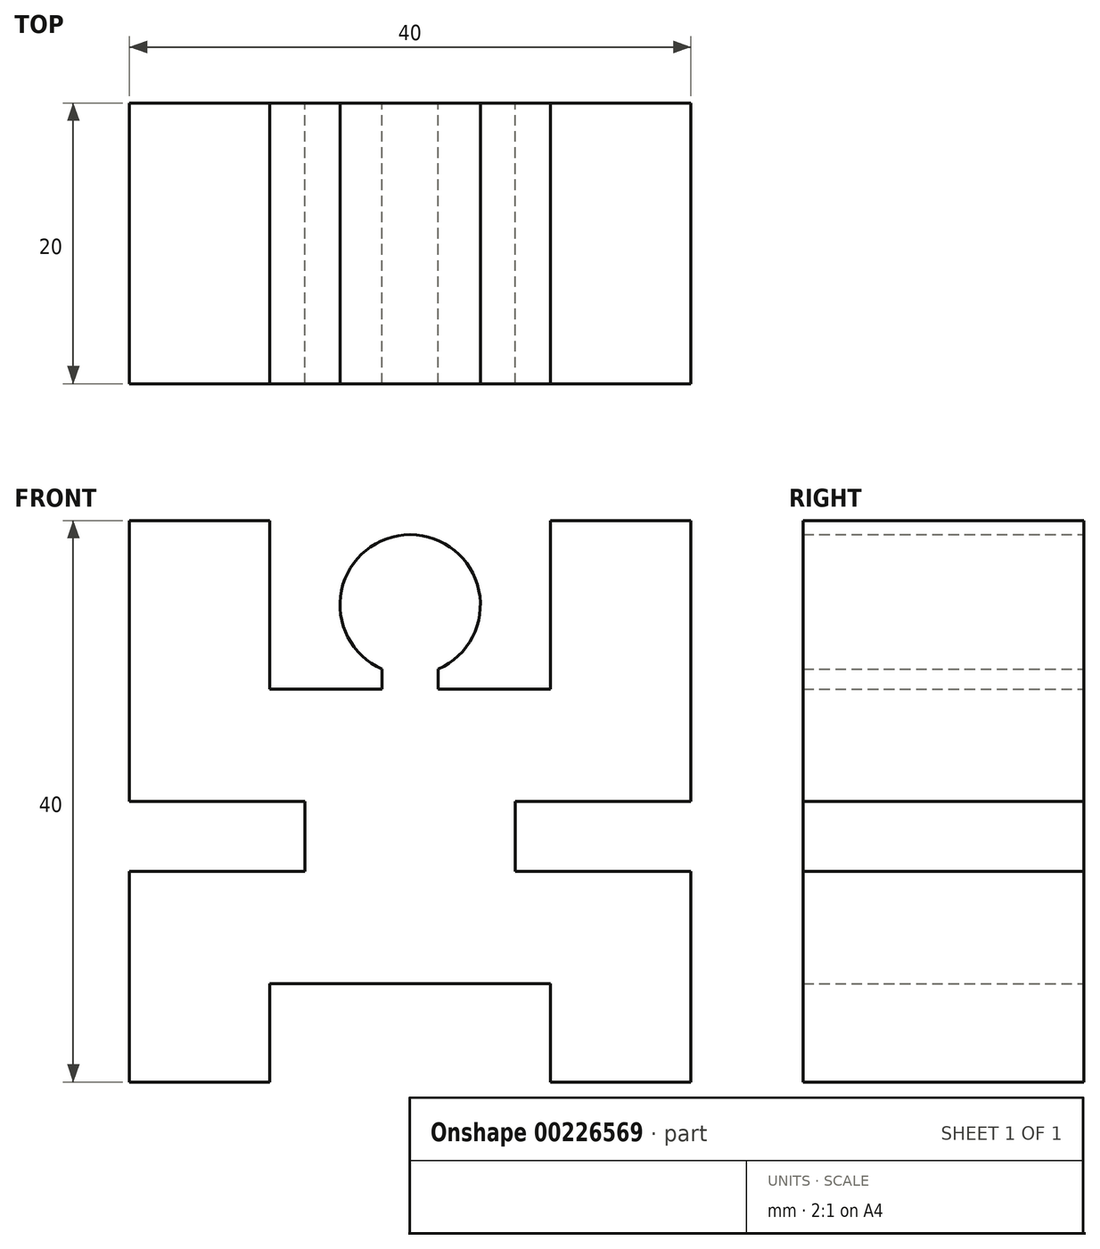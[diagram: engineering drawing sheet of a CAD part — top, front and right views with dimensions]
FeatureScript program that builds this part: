
annotation { "Feature Type Name" : "Feature", "Feature Type Description" : "" }
export const myFeature = defineFeature(function(context is Context, id is Id, definition is map)
    precondition{}
    {
        {
            var Q0;
            Q0=qCreatedBy(makeId("Front.planeOp"),FACE);
            var sketch = newSketch(context, id + "F0", { "sketchPlane" : qUnion([Q0])});
            skLineSegment(sketch, "E0", {"start": v(-2, 9.42) * mm, "end": v(-2, 8) * mm});
            skLineSegment(sketch, "E1", {"start": v(-2, 8) * mm, "end": v(-10, 8) * mm});
            skLineSegment(sketch, "E2", {"start": v(-10, 8) * mm, "end": v(-10, 20) * mm});
            skLineSegment(sketch, "E3", {"start": v(-10, 20) * mm, "end": v(-20, 20) * mm});
            skLineSegment(sketch, "E4", {"start": v(-20, 20) * mm, "end": v(-20, 0) * mm});
            skLineSegment(sketch, "E5", {"start": v(-20, 0) * mm, "end": v(-7.5, 0) * mm});
            skLineSegment(sketch, "E6", {"start": v(-7.5, 0) * mm, "end": v(-7.5, -5) * mm});
            skLineSegment(sketch, "E7", {"start": v(-7.5, -5) * mm, "end": v(-20, -5) * mm});
            skLineSegment(sketch, "E8", {"start": v(-20, -5) * mm, "end": v(-20, -20) * mm});
            skLineSegment(sketch, "E9", {"start": v(-20, -20) * mm, "end": v(-10, -20) * mm});
            skLineSegment(sketch, "E10", {"start": v(-10, -20) * mm, "end": v(-10, -13) * mm});
            skLineSegment(sketch, "E11", {"start": v(-10, -13) * mm, "end": v(10, -13) * mm});
            skLineSegment(sketch, "E12", {"start": v(10, -13) * mm, "end": v(10, -20) * mm});
            skLineSegment(sketch, "E13", {"start": v(10, -20) * mm, "end": v(20, -20) * mm});
            skLineSegment(sketch, "E14", {"start": v(20, -20) * mm, "end": v(20, -5) * mm});
            skLineSegment(sketch, "E15", {"start": v(20, -5) * mm, "end": v(7.5, -5) * mm});
            skLineSegment(sketch, "E16", {"start": v(7.5, -5) * mm, "end": v(7.5, 0) * mm});
            skLineSegment(sketch, "E17", {"start": v(7.5, 0) * mm, "end": v(20, 0) * mm});
            skLineSegment(sketch, "E18", {"start": v(20, 0) * mm, "end": v(20, 20) * mm});
            skLineSegment(sketch, "E19", {"start": v(20, 20) * mm, "end": v(10, 20) * mm});
            skLineSegment(sketch, "E20", {"start": v(10, 20) * mm, "end": v(10, 8) * mm});
            skLineSegment(sketch, "E21", {"start": v(10, 8) * mm, "end": v(2, 8) * mm});
            skLineSegment(sketch, "E22", {"start": v(2, 8) * mm, "end": v(2, 9.42) * mm});
            skArc(sketch, "E23", {"start": v(2, 9.42) * mm, "mid": v(0, 19) * mm, "end": v(-2, 9.42) * mm});
            skSolve(sketch);
        }
        {
            var Q0;
            Q0 = qSketchRegion(id + "F0", true);
            extrude(context, id + "F1", {"entities" : qUnion([Q0]), "depth" : 20 * mm});
        }
    });
